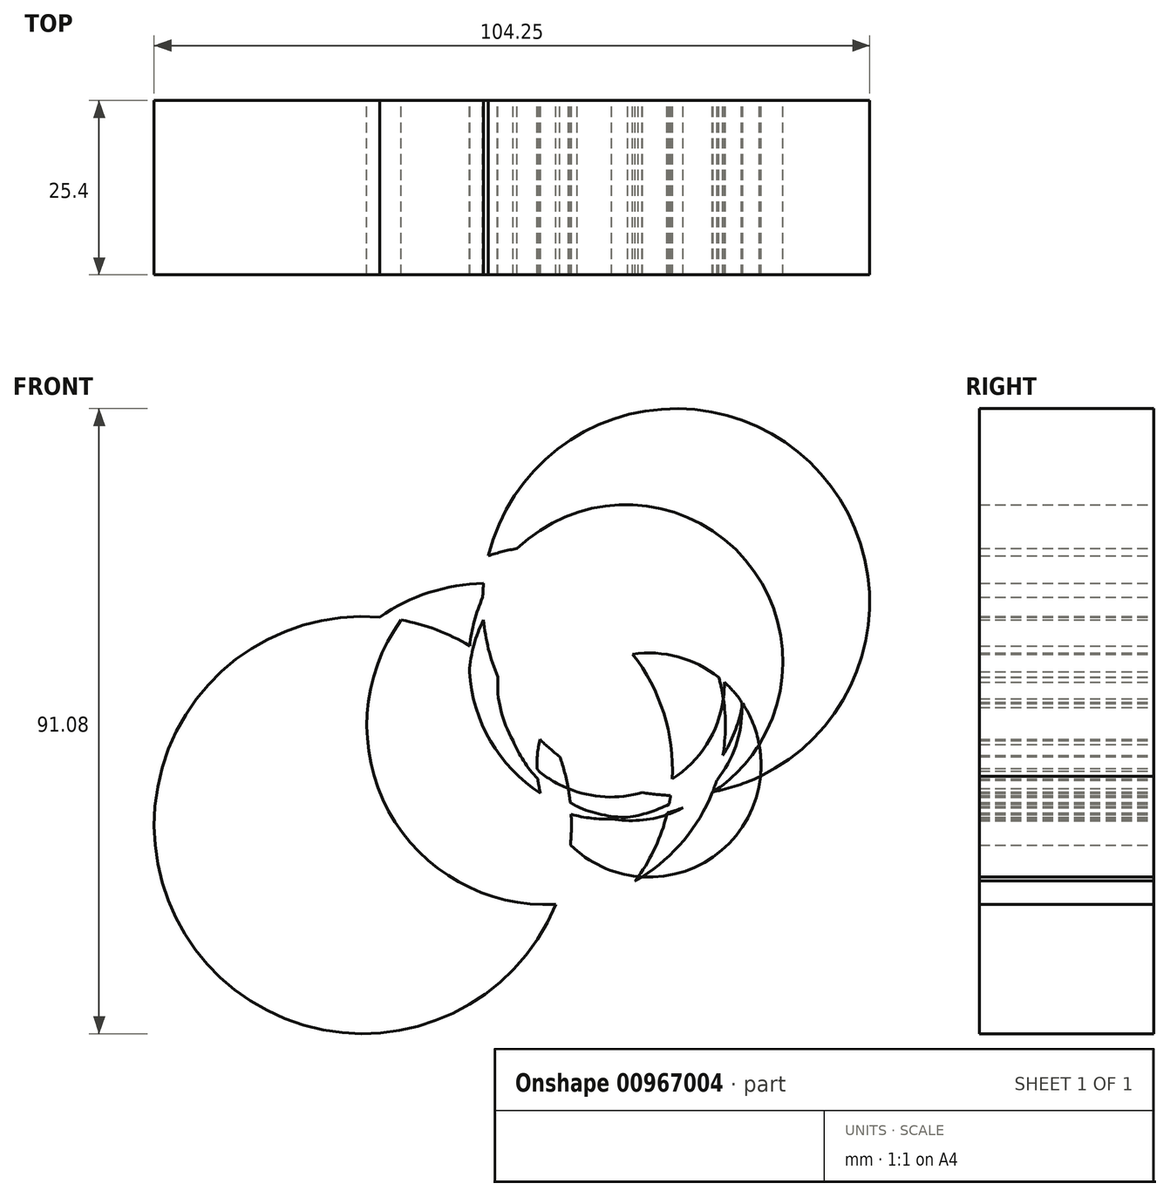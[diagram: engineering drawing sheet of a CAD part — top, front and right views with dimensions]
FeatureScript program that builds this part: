
annotation { "Feature Type Name" : "Feature", "Feature Type Description" : "" }
export const myFeature = defineFeature(function(context is Context, id is Id, definition is map)
    precondition{}
    {
        {
            var Q0;
            Q0=qCreatedBy(makeId("Front.planeOp"),FACE);
            var sketch = newSketch(context, id + "F0", { "sketchPlane" : qUnion([Q0])});
            skCircle(sketch, "E0", {"center": v(0, -47.04) * mm, "radius": 30.4 * mm});
            skCircle(sketch, "E1", {"center": v(18.03, -38.92) * mm, "radius": 27.1 * mm});
            skCircle(sketch, "E2", {"center": v(26.71, -32.52) * mm, "radius": 26.12 * mm});
            skCircle(sketch, "E3", {"center": v(45.66, -14.55) * mm, "radius": 28.19 * mm});
            skCircle(sketch, "E4", {"center": v(38.34, -23.22) * mm, "radius": 22.86 * mm});
            skCircle(sketch, "E5", {"center": v(36.16, -26.44) * mm, "radius": 16.52 * mm});
            skCircle(sketch, "E6", {"center": v(35.54, -26.1) * mm, "radius": 20.07 * mm});
            skCircle(sketch, "E7", {"center": v(39.1, -30.25) * mm, "radius": 16.15 * mm});
            skCircle(sketch, "E8", {"center": v(38.64, -27.8) * mm, "radius": 18.14 * mm});
            skCircle(sketch, "E9", {"center": v(41.7, -38.3) * mm, "radius": 16.33 * mm});
            skSolve(sketch);
        }
        {
            var Q0;
            {var subQ0=sQuery(id+"F0.wireOp",EDGE,"E9");var subQ1=sQuery(id+"F0.wireOp",EDGE,"E1");var subQ2=makeQuery(id+"F0.imprint","INTERSECT",VERTEX,{"disambiguationData":[OD(0.0)],"derivedFrom":[subQ1,subQ0]});Q0=makeQuery(id+"F0.imprint","IMPRINT",FACE,{"disambiguationData":[TD([[makeQuery(id+"F0.imprint","IMPRINT",EDGE,{"disambiguationData":[TD([[subQ2,1.0]])],"derivedFrom":subQ1}),-1.0]])]});}
            var Q1;
            {var subQ1=sQuery(id+"F0.wireOp",EDGE,"E5");var subQ5=sQuery(id+"F0.wireOp",EDGE,"E0");var subQ6=makeQuery(id+"F0.imprint","INTERSECT",VERTEX,{"disambiguationData":[OD(0.0)],"derivedFrom":[subQ5,subQ1]});Q1=makeQuery(id+"F0.imprint","IMPRINT",FACE,{"disambiguationData":[TD([[makeQuery(id+"F0.imprint","IMPRINT",EDGE,{"disambiguationData":[TD([[subQ6,-1.0]])],"derivedFrom":subQ5}),1.0]])]});}
            var Q2;
            {var subQ0=sQuery(id+"F0.wireOp",EDGE,"E1");var subQ1=sQuery(id+"F0.wireOp",EDGE,"E0");var subQ2=makeQuery(id+"F0.imprint","INTERSECT",VERTEX,{"disambiguationData":[OD(0.0)],"derivedFrom":[subQ1,subQ0]});Q2=makeQuery(id+"F0.imprint","IMPRINT",FACE,{"disambiguationData":[TD([[makeQuery(id+"F0.imprint","IMPRINT",EDGE,{"disambiguationData":[TD([[subQ2,-1.0]])],"derivedFrom":subQ1}),1.0]])]});}
            var Q3;
            {var subQ0=sQuery(id+"F0.wireOp",EDGE,"E1");var subQ1=sQuery(id+"F0.wireOp",EDGE,"E0");var subQ2=makeQuery(id+"F0.imprint","INTERSECT",VERTEX,{"disambiguationData":[OD(0.0)],"derivedFrom":[subQ1,subQ0]});Q3=makeQuery(id+"F0.imprint","IMPRINT",FACE,{"disambiguationData":[TD([[makeQuery(id+"F0.imprint","IMPRINT",EDGE,{"disambiguationData":[TD([[subQ2,1.0]])],"derivedFrom":subQ1}),1.0]])]});}
            var Q4;
            {var subQ5=sQuery(id+"F0.wireOp",EDGE,"E7");var subQ7=sQuery(id+"F0.wireOp",EDGE,"E1");var subQ8=makeQuery(id+"F0.imprint","INTERSECT",VERTEX,{"disambiguationData":[OD(0.0)],"derivedFrom":[subQ7,subQ5]});Q4=makeQuery(id+"F0.imprint","IMPRINT",FACE,{"disambiguationData":[TD([[makeQuery(id+"F0.imprint","IMPRINT",EDGE,{"disambiguationData":[TD([[subQ8,-1.0]])],"derivedFrom":subQ7}),-1.0]])]});}
            var Q5;
            {var subQ0=sQuery(id+"F0.wireOp",EDGE,"E2");var subQ1=sQuery(id+"F0.wireOp",EDGE,"E0");var subQ2=makeQuery(id+"F0.imprint","INTERSECT",VERTEX,{"disambiguationData":[OD(1.0)],"derivedFrom":[subQ1,subQ0]});Q5=makeQuery(id+"F0.imprint","IMPRINT",FACE,{"disambiguationData":[TD([[makeQuery(id+"F0.imprint","IMPRINT",EDGE,{"disambiguationData":[TD([[subQ2,-1.0]])],"derivedFrom":subQ1}),-1.0]])]});}
            var Q6;
            {var subQ0=sQuery(id+"F0.wireOp",EDGE,"E5");var subQ1=sQuery(id+"F0.wireOp",EDGE,"E1");var subQ2=makeQuery(id+"F0.imprint","INTERSECT",VERTEX,{"disambiguationData":[OD(0.0)],"derivedFrom":[subQ1,subQ0]});Q6=makeQuery(id+"F0.imprint","IMPRINT",FACE,{"disambiguationData":[TD([[makeQuery(id+"F0.imprint","IMPRINT",EDGE,{"disambiguationData":[TD([[subQ2,-1.0]])],"derivedFrom":subQ1}),-1.0]])]});}
            var Q7;
            {var subQ0=sQuery(id+"F0.wireOp",EDGE,"E8");var subQ1=sQuery(id+"F0.wireOp",EDGE,"E2");var subQ2=makeQuery(id+"F0.imprint","INTERSECT",VERTEX,{"disambiguationData":[OD(0.0)],"derivedFrom":[subQ1,subQ0]});Q7=makeQuery(id+"F0.imprint","IMPRINT",FACE,{"disambiguationData":[TD([[makeQuery(id+"F0.imprint","IMPRINT",EDGE,{"disambiguationData":[TD([[subQ2,-1.0]])],"derivedFrom":subQ1}),-1.0]])]});}
            var Q8;
            {var subQ0=sQuery(id+"F0.wireOp",EDGE,"E3");var subQ1=sQuery(id+"F0.wireOp",EDGE,"E2");var subQ2=makeQuery(id+"F0.imprint","INTERSECT",VERTEX,{"disambiguationData":[OD(0.0)],"derivedFrom":[subQ1,subQ0]});Q8=makeQuery(id+"F0.imprint","IMPRINT",FACE,{"disambiguationData":[TD([[makeQuery(id+"F0.imprint","IMPRINT",EDGE,{"disambiguationData":[TD([[subQ2,1.0]])],"derivedFrom":subQ1}),-1.0]])]});}
            var Q9;
            {var subQ1=sQuery(id+"F0.wireOp",EDGE,"E6");var subQ5=sQuery(id+"F0.wireOp",EDGE,"E2");var subQ6=makeQuery(id+"F0.imprint","INTERSECT",VERTEX,{"disambiguationData":[OD(0.0)],"derivedFrom":[subQ5,subQ1]});Q9=makeQuery(id+"F0.imprint","IMPRINT",FACE,{"disambiguationData":[TD([[makeQuery(id+"F0.imprint","IMPRINT",EDGE,{"disambiguationData":[TD([[subQ6,-1.0]])],"derivedFrom":subQ5}),-1.0]])]});}
            var Q10;
            {var subQ1=sQuery(id+"F0.wireOp",EDGE,"E2");var subQ6=sQuery(id+"F0.wireOp",EDGE,"E3");var subQ9=makeQuery(id+"F0.imprint","INTERSECT",VERTEX,{"disambiguationData":[OD(1.0)],"derivedFrom":[subQ1,subQ6]});Q10=makeQuery(id+"F0.imprint","IMPRINT",FACE,{"disambiguationData":[TD([[makeQuery(id+"F0.imprint","IMPRINT",EDGE,{"disambiguationData":[TD([[subQ9,-1.0]])],"derivedFrom":subQ1}),-1.0]])]});}
            var Q11;
            {var subQ0=sQuery(id+"F0.wireOp",EDGE,"E9");var subQ1=sQuery(id+"F0.wireOp",EDGE,"E2");var subQ2=makeQuery(id+"F0.imprint","INTERSECT",VERTEX,{"disambiguationData":[OD(0.0)],"derivedFrom":[subQ1,subQ0]});Q11=makeQuery(id+"F0.imprint","IMPRINT",FACE,{"disambiguationData":[TD([[makeQuery(id+"F0.imprint","IMPRINT",EDGE,{"disambiguationData":[TD([[subQ2,-1.0]])],"derivedFrom":subQ1}),-1.0]])]});}
            var Q12;
            {var subQ1=sQuery(id+"F0.wireOp",EDGE,"E0");var subQ11=sQuery(id+"F0.wireOp",EDGE,"E7");var subQ13=makeQuery(id+"F0.imprint","INTERSECT",VERTEX,{"disambiguationData":[OD(0.0)],"derivedFrom":[subQ1,subQ11]});Q12=makeQuery(id+"F0.imprint","IMPRINT",FACE,{"disambiguationData":[TD([[makeQuery(id+"F0.imprint","IMPRINT",EDGE,{"disambiguationData":[TD([[subQ13,-1.0]])],"derivedFrom":subQ1}),-1.0]])]});}
            var Q13;
            {var subQ1=sQuery(id+"F0.wireOp",EDGE,"E3");var subQ10=sQuery(id+"F0.wireOp",EDGE,"E0");var subQ11=makeQuery(id+"F0.imprint","INTERSECT",VERTEX,{"disambiguationData":[OD(1.0)],"derivedFrom":[subQ10,subQ1]});Q13=makeQuery(id+"F0.imprint","IMPRINT",FACE,{"disambiguationData":[TD([[makeQuery(id+"F0.imprint","IMPRINT",EDGE,{"disambiguationData":[TD([[subQ11,-1.0]])],"derivedFrom":subQ10}),1.0]])]});}
            var Q14;
            {var subQ0=sQuery(id+"F0.wireOp",EDGE,"E9");var subQ1=sQuery(id+"F0.wireOp",EDGE,"E0");var subQ2=makeQuery(id+"F0.imprint","INTERSECT",VERTEX,{"disambiguationData":[OD(0.0)],"derivedFrom":[subQ1,subQ0]});Q14=makeQuery(id+"F0.imprint","IMPRINT",FACE,{"disambiguationData":[TD([[makeQuery(id+"F0.imprint","IMPRINT",EDGE,{"disambiguationData":[TD([[subQ2,-1.0]])],"derivedFrom":subQ1}),-1.0]])]});}
            var Q15;
            {var subQ0=sQuery(id+"F0.wireOp",EDGE,"E3");var subQ1=sQuery(id+"F0.wireOp",EDGE,"E0");var subQ2=makeQuery(id+"F0.imprint","INTERSECT",VERTEX,{"disambiguationData":[OD(1.0)],"derivedFrom":[subQ1,subQ0]});Q15=makeQuery(id+"F0.imprint","IMPRINT",FACE,{"disambiguationData":[TD([[makeQuery(id+"F0.imprint","IMPRINT",EDGE,{"disambiguationData":[TD([[subQ2,-1.0]])],"derivedFrom":subQ1}),-1.0]])]});}
            var Q16;
            {var subQ3=sQuery(id+"F0.wireOp",EDGE,"E4");var subQ7=sQuery(id+"F0.wireOp",EDGE,"E0");var subQ9=makeQuery(id+"F0.imprint","INTERSECT",VERTEX,{"disambiguationData":[OD(1.0)],"derivedFrom":[subQ7,subQ3]});Q16=makeQuery(id+"F0.imprint","IMPRINT",FACE,{"disambiguationData":[TD([[makeQuery(id+"F0.imprint","IMPRINT",EDGE,{"disambiguationData":[TD([[subQ9,-1.0]])],"derivedFrom":subQ7}),-1.0]])]});}
            var Q17;
            {var subQ0=sQuery(id+"F0.wireOp",EDGE,"E6");var subQ1=sQuery(id+"F0.wireOp",EDGE,"E1");var subQ2=makeQuery(id+"F0.imprint","INTERSECT",VERTEX,{"disambiguationData":[OD(0.0)],"derivedFrom":[subQ1,subQ0]});Q17=makeQuery(id+"F0.imprint","IMPRINT",FACE,{"disambiguationData":[TD([[makeQuery(id+"F0.imprint","IMPRINT",EDGE,{"disambiguationData":[TD([[subQ2,-1.0]])],"derivedFrom":subQ1}),1.0]])]});}
            extrude(context, id + "F1", {"entities" : qUnion([Q0, Q1, Q2, Q3, Q4, Q5, Q6, Q7, Q8, Q9, Q10, Q11, Q12, Q13, Q14, Q15, Q16, Q17]), "depth" : 25.4 * mm, "offsetDistance" : 25.4 * mm});
        }
    });
